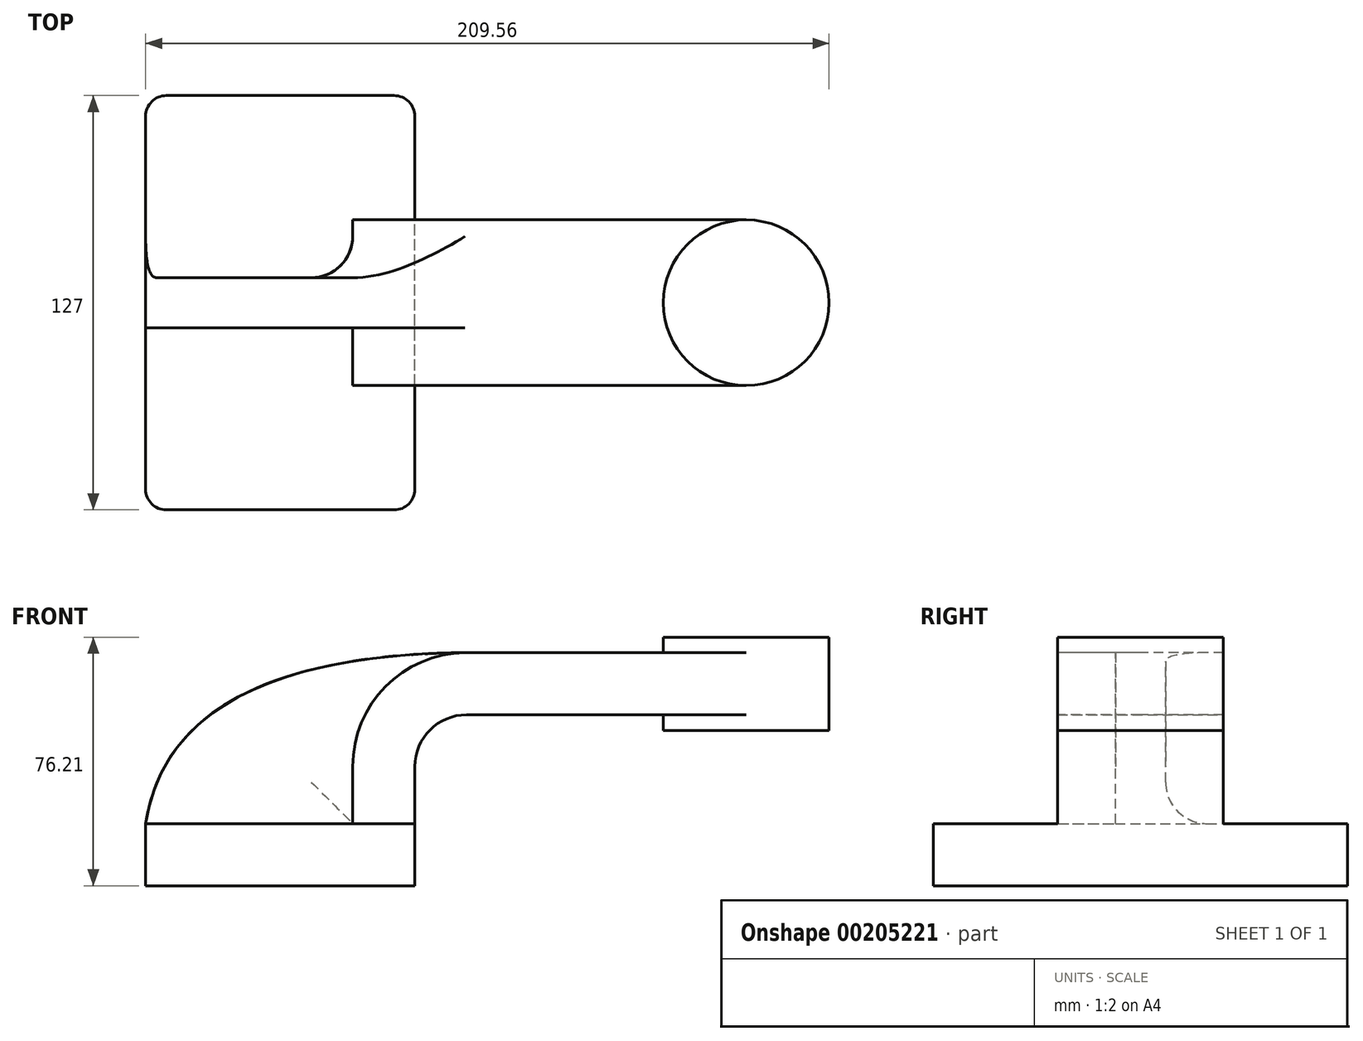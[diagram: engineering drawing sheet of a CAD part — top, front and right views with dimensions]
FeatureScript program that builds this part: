
annotation { "Feature Type Name" : "Feature", "Feature Type Description" : "" }
export const myFeature = defineFeature(function(context is Context, id is Id, definition is map)
    precondition{}
    {
        {
            var Q0;
            Q0=qCreatedBy(makeId("Front.planeOp"),FACE);
            var sketch = newSketch(context, id + "F0", { "sketchPlane" : qUnion([Q0])});
            skLineSegment(sketch, "E0.bottom", {"start": v(-41.28, -9.53) * mm, "end": v(41.28, -9.53) * mm});
            skLineSegment(sketch, "E0.top", {"start": v(-41.28, 9.53) * mm, "end": v(41.28, 9.53) * mm});
            skLineSegment(sketch, "E0.left", {"start": v(-41.28, -9.53) * mm, "end": v(-41.28, 9.53) * mm});
            skLineSegment(sketch, "E0.right", {"start": v(41.28, -9.53) * mm, "end": v(41.28, 9.53) * mm});
            skPoint(sketch, "E0.middle", {"position": v(0, 0) * mm});
            skLineSegment(sketch, "E1.bottom", {"start": v(168.28, 38.1) * mm, "end": v(117.48, 38.1) * mm});
            skLineSegment(sketch, "E1.top", {"start": v(168.28, 66.68) * mm, "end": v(117.48, 66.67) * mm});
            skLineSegment(sketch, "E1.left", {"start": v(168.28, 38.1) * mm, "end": v(168.28, 66.68) * mm});
            skLineSegment(sketch, "E1.right", {"start": v(117.48, 38.1) * mm, "end": v(117.48, 66.68) * mm});
            skPoint(sketch, "E1.middle", {"position": v(142.88, 52.39) * mm});
            skLineSegment(sketch, "E2", {"start": v(41.28, 9.53) * mm, "end": v(41.28, 27) * mm});
            skArc(sketch, "E3", {"start": v(41.28, 27) * mm, "mid": v(45.92, 38.23) * mm, "end": v(57.15, 42.88) * mm});
            skLineSegment(sketch, "E4", {"start": v(57.15, 42.88) * mm, "end": v(142.88, 42.88) * mm});
            skLineSegment(sketch, "E5.0", {"start": v(57.15, 61.93) * mm, "end": v(142.88, 61.93) * mm});
            skArc(sketch, "E5.1", {"start": v(22.23, 27) * mm, "mid": v(32.45, 51.7) * mm, "end": v(57.15, 61.93) * mm});
            skLineSegment(sketch, "E5.2", {"start": v(22.23, 9.53) * mm, "end": v(22.23, 27) * mm});
            skFitSpline(sketch, "E6", {"points": [v(-41.28, 9.53) * mm, v(57.15, 61.93) * mm], "startDerivative": vector(19.2, 128.41) * mm, "endDerivative": vector(129.1, 0.8) * mm});
            skLineSegment(sketch, "E7", {"start": v(142.88, 38.1) * mm, "end": v(142.88, 66.68) * mm});
            skSolve(sketch);
        }
        {
            var Q0;
            Q0=makeQuery(id+"F0.imprint","IMPRINT",FACE,{"disambiguationData":[TD([[makeQuery(id+"F0.imprint","IMPRINT",EDGE,{"derivedFrom":sQuery(id+"F0.wireOp",EDGE,"E0.bottom")}),1.0]])]});
            extrude(context, id + "F1", {"entities" : qUnion([Q0]), "endBound" : BoundingType.SYMMETRIC, "depth" : 127 * mm});
        }
        {
            var Q0;
            {var subQ1=sQuery(id+"F0.wireOp",EDGE,"E2");Q0=makeQuery(id+"F0.imprint","IMPRINT",FACE,{"disambiguationData":[TD([[makeQuery(id+"F0.imprint","IMPRINT",EDGE,{"derivedFrom":subQ1}),1.0]])]});}
            var Q1;
            {var subQ0=sQuery(id+"F0.wireOp",EDGE,"E4");var subQ1=sQuery(id+"F0.wireOp",EDGE,"E1.right");var subQ2=makeQuery(id+"F0.imprint","INTERSECT",VERTEX,{"derivedFrom":[subQ1,subQ0]});Q1=makeQuery(id+"F0.imprint","IMPRINT",FACE,{"disambiguationData":[TD([[makeQuery(id+"F0.imprint","IMPRINT",EDGE,{"disambiguationData":[TD([[subQ2,-1.0]])],"derivedFrom":subQ1}),-1.0]])]});}
            extrude(context, id + "F2", {"entities" : qUnion([Q0, Q1]), "operationType" : NewBodyOperationType.ADD, "endBound" : BoundingType.SYMMETRIC, "depth" : 50.8 * mm});
        }
        {
            var Q0;
            {var subQ3=sQuery(id+"F0.wireOp",EDGE,"E5.2");Q0=makeQuery(id+"F0.imprint","IMPRINT",FACE,{"disambiguationData":[TD([[makeQuery(id+"F0.imprint","IMPRINT",EDGE,{"derivedFrom":subQ3}),1.0]])]});}
            extrude(context, id + "F3", {"entities" : qUnion([Q0]), "operationType" : NewBodyOperationType.ADD, "endBound" : BoundingType.SYMMETRIC, "depth" : 15.37 * mm});
        }
        {
            var Q0;
            {var subQ4=sQuery(id+"F0.wireOp",EDGE,"E1.left");Q0=makeQuery(id+"F0.imprint","IMPRINT",FACE,{"disambiguationData":[TD([[makeQuery(id+"F0.imprint","IMPRINT",EDGE,{"derivedFrom":subQ4}),1.0]])]});}
            var Q1;
            Q1=sQuery(id+"F0.wireOp",EDGE,"E7");
            revolve(context, id + "F4", {"operationType" : NewBodyOperationType.ADD, "entities" : qUnion([Q0]), "axis" : qUnion([Q1]), "revolveType" : RevolveType.FULL});
        }
        {
            var Q0;
            Q0=makeQuery(id+"F1.opExtrude","CAP_EDGE",EDGE,{"disambiguationData":[OSD([sQuery(id+"F0.wireOp",EDGE,"E0.left")])],"isStart":false});
            var Q1;
            Q1=makeQuery(id+"F1.opExtrude","CAP_EDGE",EDGE,{"disambiguationData":[OSD([sQuery(id+"F0.wireOp",EDGE,"E0.right")])],"isStart":false});
            var Q2;
            Q2=makeQuery(id+"F1.opExtrude","CAP_EDGE",EDGE,{"disambiguationData":[OSD([sQuery(id+"F0.wireOp",EDGE,"E0.right")])],"isStart":true});
            var Q3;
            Q3=makeQuery(id+"F1.opExtrude","CAP_EDGE",EDGE,{"disambiguationData":[OSD([sQuery(id+"F0.wireOp",EDGE,"E0.left")])],"isStart":true});
            fillet(context, id + "F5", {"entities" : qUnion([Q0, Q1, Q2, Q3]), "radius" : 6.35 * mm, "tangentPropagation" : true, "allowEdgeOverflow" : false});
        }
        {
            var Q0;
            Q0=makeQuery(id+"F3.opExtrude","CAP_EDGE",EDGE,{"disambiguationData":[OSD([sQuery(id+"F0.wireOp",EDGE,"E0.top")])],"isStart":true});
            var Q1;
            Q1=makeQuery(id+"F3.opExtrude","CAP_EDGE",EDGE,{"disambiguationData":[OSD([sQuery(id+"F0.wireOp",EDGE,"E0.top")])],"isStart":false});
            var Q2;
            Q2=makeQuery(id+"F3.opExtrude","CAP_EDGE",EDGE,{"disambiguationData":[OSD([sQuery(id+"F0.wireOp",EDGE,"E5.1")])],"isStart":false});
            var Q3;
            Q3=makeQuery(id+"F3.opExtrude","CAP_EDGE",EDGE,{"disambiguationData":[OSD([sQuery(id+"F0.wireOp",EDGE,"E5.2")])],"isStart":false});
            var Q4;
            {var subQ0=sQuery(id+"F0.wireOp",EDGE,"E0.top");var subQ1=sQuery(id+"F0.wireOp",EDGE,"E6");var subQ2=sQuery(id+"F0.wireOp",EDGE,"E5.2");var subQ3=sQuery(id+"F0.wireOp",EDGE,"E5.1");Q4=makeQuery(id+"F3.boolean.opBoolean","SPLIT",EDGE,{"disambiguationData":[TD([makeQuery(id+"F3.opExtrude","CAP_FACE",FACE,{"disambiguationData":[OSD([subQ0,subQ3,subQ2,subQ1])],"isStart":false})])],"derivedFrom":makeQuery(id+"F2.opExtrude","SWEPT_EDGE",EDGE,{"disambiguationData":[OSD([subQ0,subQ2])]})});}
            var Q5;
            Q5=makeQuery(id+"F3.opExtrude","CAP_EDGE",EDGE,{"disambiguationData":[OSD([sQuery(id+"F0.wireOp",EDGE,"E5.1")])],"isStart":true});
            var Q6;
            Q6=makeQuery(id+"F3.opExtrude","CAP_EDGE",EDGE,{"disambiguationData":[OSD([sQuery(id+"F0.wireOp",EDGE,"E5.2")])],"isStart":true});
            var Q7;
            {var subQ0=sQuery(id+"F0.wireOp",EDGE,"E0.top");var subQ1=sQuery(id+"F0.wireOp",EDGE,"E6");var subQ2=sQuery(id+"F0.wireOp",EDGE,"E5.2");var subQ3=sQuery(id+"F0.wireOp",EDGE,"E5.1");Q7=makeQuery(id+"F3.boolean.opBoolean","SPLIT",EDGE,{"disambiguationData":[TD([makeQuery(id+"F3.opExtrude","CAP_FACE",FACE,{"disambiguationData":[OSD([subQ0,subQ3,subQ2,subQ1])],"isStart":true})])],"derivedFrom":makeQuery(id+"F2.opExtrude","SWEPT_EDGE",EDGE,{"disambiguationData":[OSD([subQ0,subQ2])]})});}
            fillet(context, id + "F6", {"entities" : qUnion([Q0, Q1, Q2, Q3, Q4, Q5, Q6, Q7]), "radius" : 12.7 * mm, "tangentPropagation" : true, "allowEdgeOverflow" : false});
        }
    });
